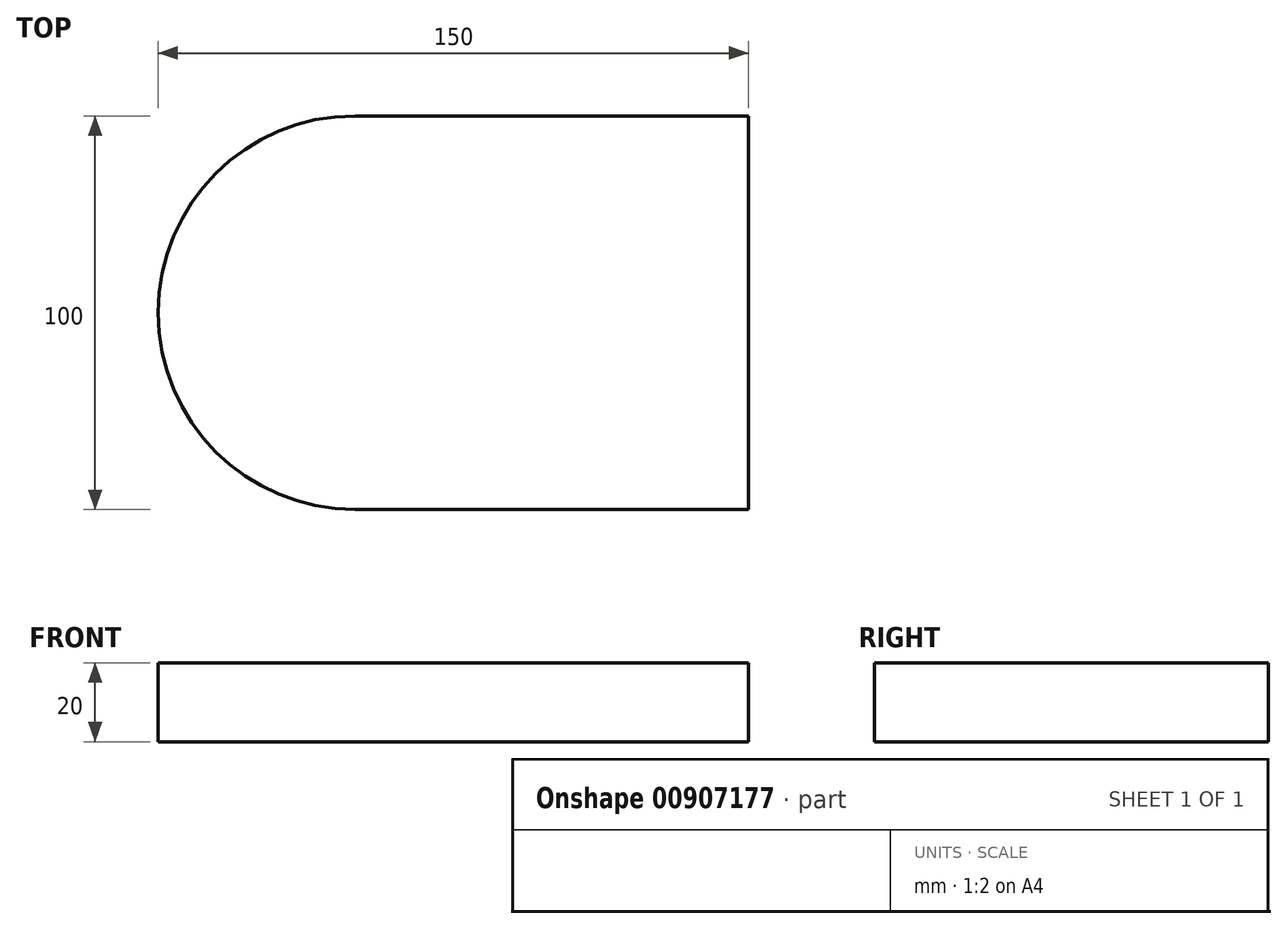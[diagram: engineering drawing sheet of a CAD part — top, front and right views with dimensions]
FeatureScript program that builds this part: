
annotation { "Feature Type Name" : "Feature", "Feature Type Description" : "" }
export const myFeature = defineFeature(function(context is Context, id is Id, definition is map)
    precondition{}
    {
        {
            var Q0;
            Q0=qCreatedBy(makeId("Top.planeOp"),FACE);
            var sketch = newSketch(context, id + "F0", { "sketchPlane" : qUnion([Q0])});
            skArc(sketch, "E0", {"start": v(0, 50) * mm, "mid": v(-50, 0) * mm, "end": v(0, -50) * mm});
            skLineSegment(sketch, "E1", {"start": v(0, -50) * mm, "end": v(100, -50) * mm});
            skLineSegment(sketch, "E2", {"start": v(100, -50) * mm, "end": v(100, 0) * mm});
            skLineSegment(sketch, "E3", {"start": v(0, 50) * mm, "end": v(100, 50) * mm});
            skLineSegment(sketch, "E4", {"start": v(100, 50) * mm, "end": v(100, 0) * mm});
            skSolve(sketch);
        }
        {
            var Q0;
            Q0=makeQuery(id+"F0.imprint","IMPRINT",FACE,{"disambiguationData":[TD([[makeQuery(id+"F0.imprint","IMPRINT",EDGE,{"derivedFrom":sQuery(id+"F0.wireOp",EDGE,"E0")}),1.0]])]});
            extrude(context, id + "F1", {"entities" : qUnion([Q0]), "depth" : 20 * mm, "offsetDistance" : 25 * mm});
        }
    });
